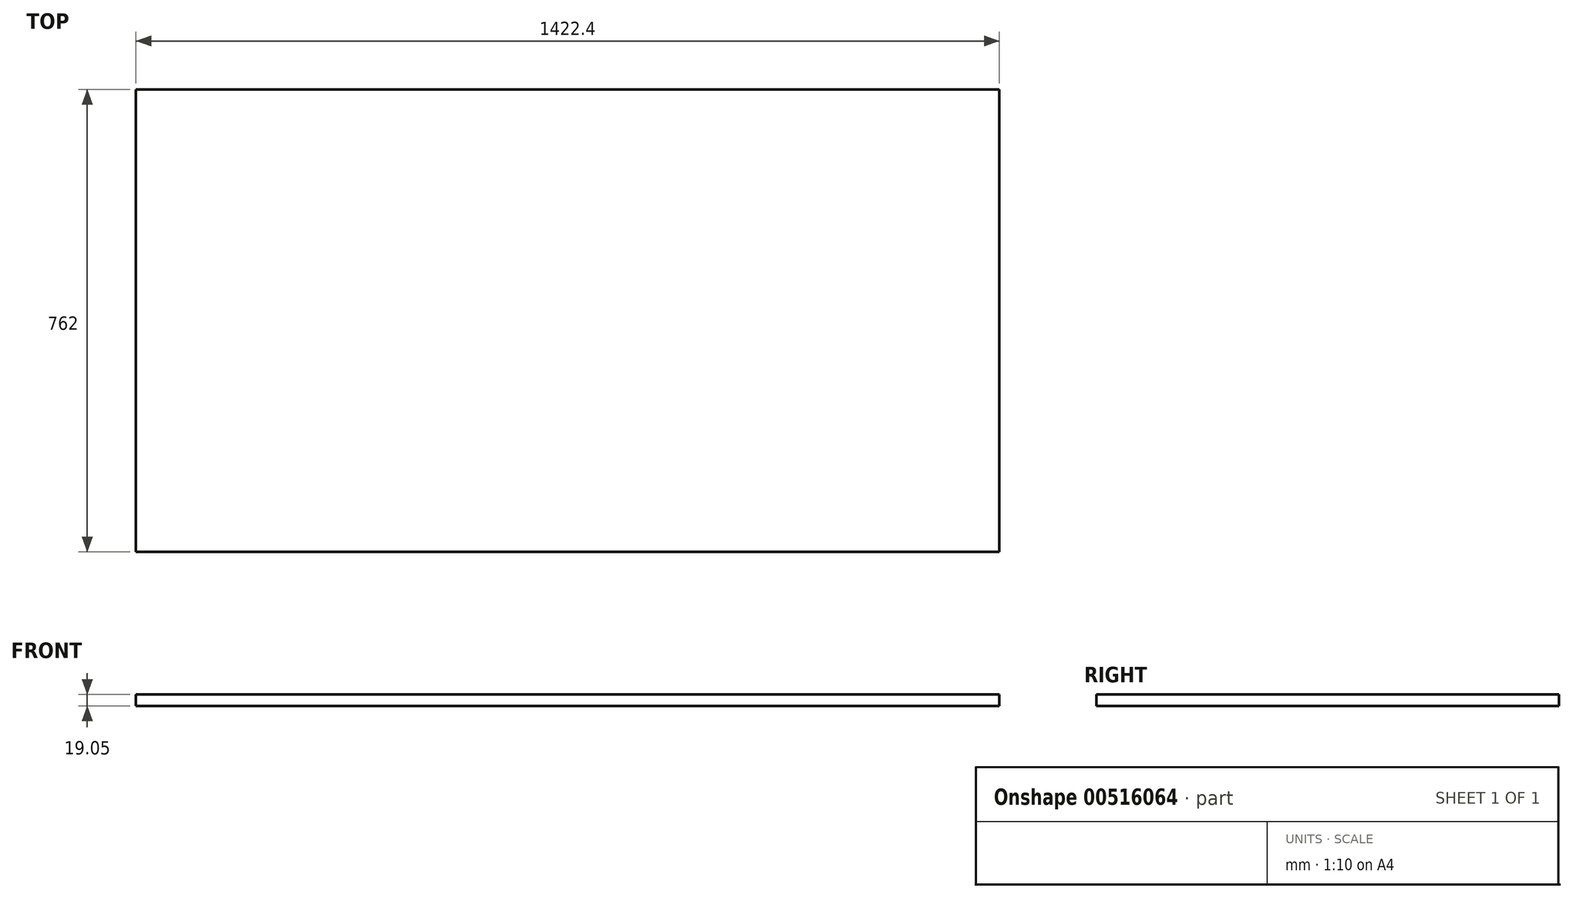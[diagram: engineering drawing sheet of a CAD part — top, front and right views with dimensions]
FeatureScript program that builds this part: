
annotation { "Feature Type Name" : "Feature", "Feature Type Description" : "" }
export const myFeature = defineFeature(function(context is Context, id is Id, definition is map)
    precondition{}
    {
        {
            var Q0;
            Q0=qCreatedBy(makeId("Top.planeOp"),FACE);
            var sketch = newSketch(context, id + "F0", { "sketchPlane" : qUnion([Q0])});
            skLineSegment(sketch, "E0.bottom", {"start": v(-711.2, -381) * mm, "end": v(711.2, -381) * mm});
            skLineSegment(sketch, "E0.top", {"start": v(-711.2, 381) * mm, "end": v(711.2, 381) * mm});
            skLineSegment(sketch, "E0.left", {"start": v(-711.2, -381) * mm, "end": v(-711.2, 381) * mm});
            skLineSegment(sketch, "E0.right", {"start": v(711.2, -381) * mm, "end": v(711.2, 381) * mm});
            skPoint(sketch, "E0.middle", {"position": v(0, 0) * mm});
            skSolve(sketch);
        }
        {
            var Q0;
            Q0=makeQuery(id+"F0.imprint","IMPRINT",FACE,{"disambiguationData":[TD([[makeQuery(id+"F0.imprint","IMPRINT",EDGE,{"derivedFrom":sQuery(id+"F0.wireOp",EDGE,"E0.bottom")}),1.0]])]});
            extrude(context, id + "F1", {"entities" : qUnion([Q0]), "depth" : 19.05 * mm, "offsetDistance" : 25.4 * mm});
        }
    });
